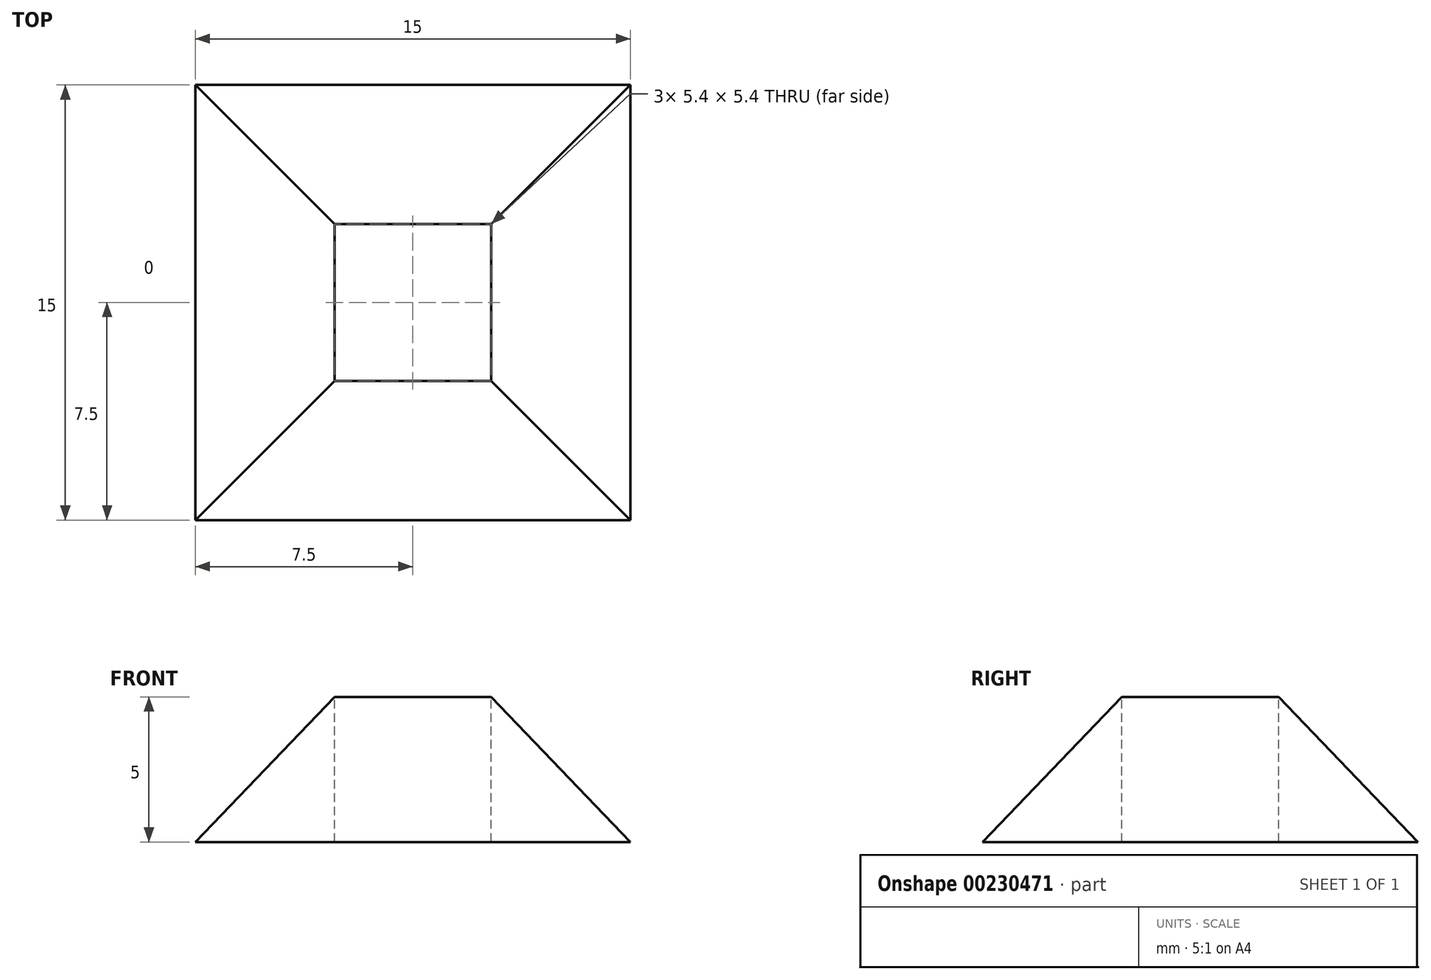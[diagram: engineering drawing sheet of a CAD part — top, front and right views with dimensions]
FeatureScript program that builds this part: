
annotation { "Feature Type Name" : "Feature", "Feature Type Description" : "" }
export const myFeature = defineFeature(function(context is Context, id is Id, definition is map)
    precondition{}
    {
        {
            var Q0;
            Q0=qCreatedBy(makeId("Top.planeOp"),FACE);
            var sketch = newSketch(context, id + "F0", { "sketchPlane" : qUnion([Q0])});
            skLineSegment(sketch, "E0.bottom", {"start": v(7.5, 7.5) * mm, "end": v(-7.5, 7.5) * mm});
            skLineSegment(sketch, "E0.top", {"start": v(7.5, -7.5) * mm, "end": v(-7.5, -7.5) * mm});
            skLineSegment(sketch, "E0.left", {"start": v(7.5, 7.5) * mm, "end": v(7.5, -7.5) * mm});
            skLineSegment(sketch, "E0.right", {"start": v(-7.5, 7.5) * mm, "end": v(-7.5, -7.5) * mm});
            skPoint(sketch, "E0.middle", {"position": v(0, 0) * mm});
            skSolve(sketch);
        }
        {
            var Q0;
            Q0=makeQuery(id+"F0.imprint","IMPRINT",FACE,{"disambiguationData":[TD([[makeQuery(id+"F0.imprint","IMPRINT",EDGE,{"derivedFrom":sQuery(id+"F0.wireOp",EDGE,"E0.bottom")}),1.0]])]});
            cPlane(context, id + "F1", {"entities" : qUnion([Q0]), "cplaneType" : CPlaneType.OFFSET, "offset" : 5 * mm, "width" : 150 * mm, "height" : 150 * mm});
        }
        {
            var Q0;
            Q0=qCreatedBy(id+"F1.planeOp",FACE);
            var sketch = newSketch(context, id + "F2", { "sketchPlane" : qUnion([Q0])});
            skLineSegment(sketch, "E1.bottom", {"start": v(2.7, 2.7) * mm, "end": v(-2.7, 2.7) * mm});
            skLineSegment(sketch, "E1.top", {"start": v(2.7, -2.7) * mm, "end": v(-2.7, -2.7) * mm});
            skLineSegment(sketch, "E1.left", {"start": v(2.7, 2.7) * mm, "end": v(2.7, -2.7) * mm});
            skLineSegment(sketch, "E1.right", {"start": v(-2.7, 2.7) * mm, "end": v(-2.7, -2.7) * mm});
            skPoint(sketch, "E1.middle", {"position": v(0, 0) * mm});
            skSolve(sketch);
        }
        {
            var Q0;
            Q0=makeQuery(id+"F0.imprint","IMPRINT",FACE,{"disambiguationData":[TD([[makeQuery(id+"F0.imprint","IMPRINT",EDGE,{"derivedFrom":sQuery(id+"F0.wireOp",EDGE,"E0.bottom")}),1.0]])]});
            var Q1;
            Q1=makeQuery(id+"F2.imprint","IMPRINT",FACE,{"disambiguationData":[TD([[makeQuery(id+"F2.imprint","IMPRINT",EDGE,{"derivedFrom":sQuery(id+"F2.wireOp",EDGE,"E1.bottom")}),1.0]])]});
            loft(context, id + "F3", {"sheetProfilesArray" : [{ "sheetProfileEntities" : qUnion([Q0]) }, { "sheetProfileEntities" : qUnion([Q1]) }]});
        }
        {
            var Q0;
            Q0=makeQuery(id+"F2.imprint","IMPRINT",FACE,{"disambiguationData":[TD([[makeQuery(id+"F2.imprint","IMPRINT",EDGE,{"derivedFrom":sQuery(id+"F2.wireOp",EDGE,"E1.bottom")}),1.0]])]});
            extrude(context, id + "F4", {"entities" : qUnion([Q0]), "operationType" : NewBodyOperationType.REMOVE, "endBound" : BoundingType.UP_TO_NEXT, "oppositeDirection" : true, "depth" : 25 * mm});
        }
    });
